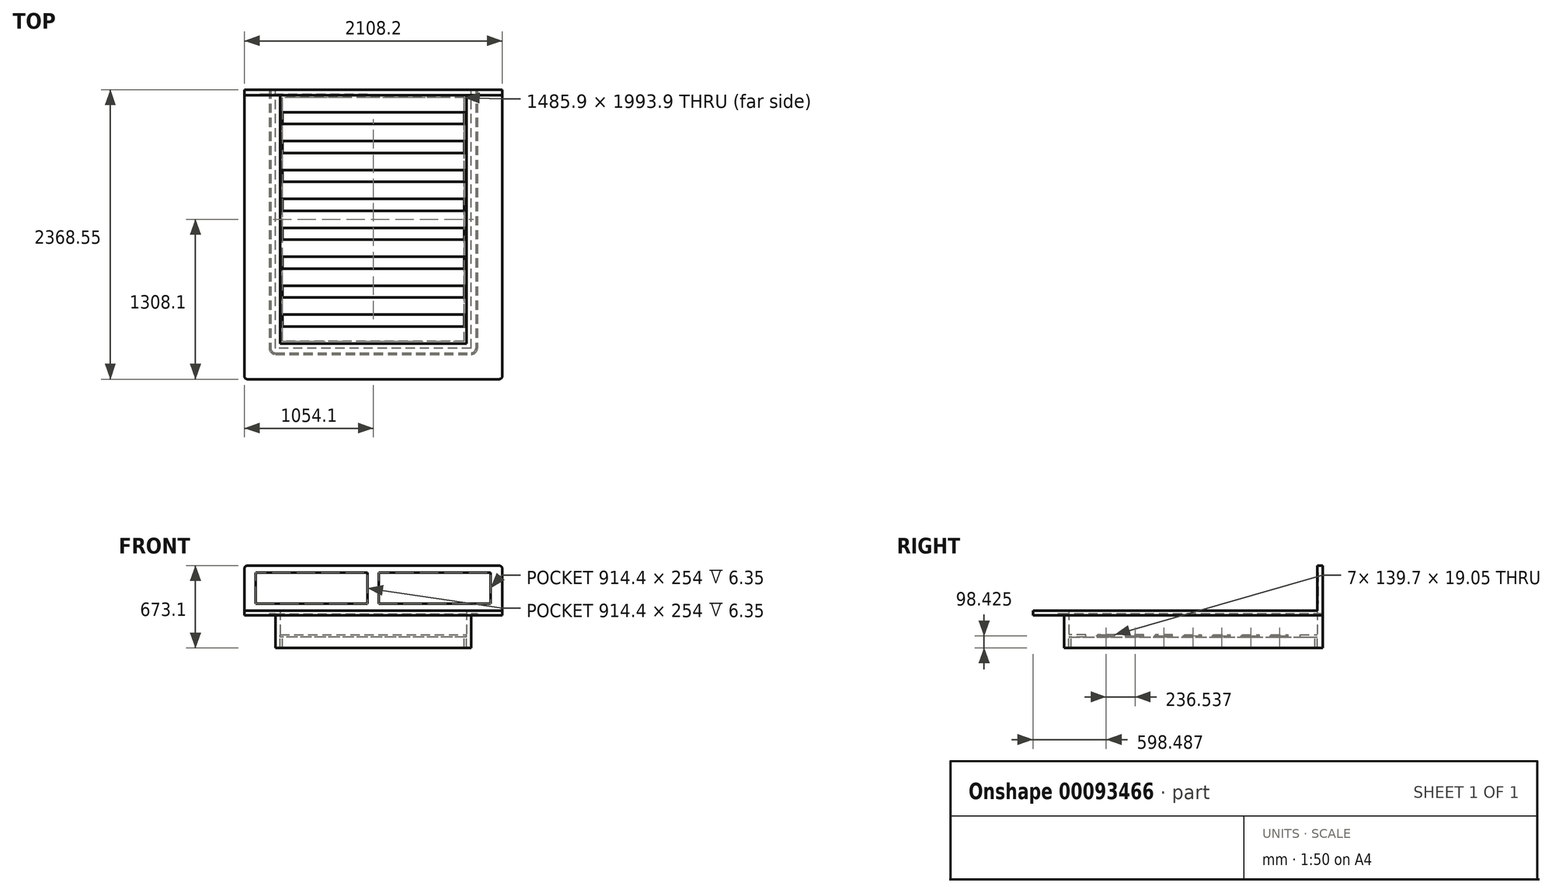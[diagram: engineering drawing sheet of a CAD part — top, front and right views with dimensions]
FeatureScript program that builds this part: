
annotation { "Feature Type Name" : "Feature", "Feature Type Description" : "" }
export const myFeature = defineFeature(function(context is Context, id is Id, definition is map)
    precondition{}
    {
        {
            var Q0;
            Q0=qCreatedBy(makeId("Top.planeOp"),FACE);
            var sketch = newSketch(context, id + "F0", { "sketchPlane" : qUnion([Q0])});
            skLineSegment(sketch, "E0.bottom", {"start": v(762, -1016) * mm, "end": v(-762, -1016) * mm});
            skLineSegment(sketch, "E0.top", {"start": v(762, 1016) * mm, "end": v(-762, 1016) * mm});
            skLineSegment(sketch, "E0.left", {"start": v(762, -1016) * mm, "end": v(762, 1016) * mm});
            skLineSegment(sketch, "E0.right", {"start": v(-762, -1016) * mm, "end": v(-762, 1016) * mm});
            skPoint(sketch, "E0.middle", {"position": v(0, 0) * mm});
            skLineSegment(sketch, "E1.bottom", {"start": v(800.1, -1054.1) * mm, "end": v(-800.1, -1054.1) * mm});
            skLineSegment(sketch, "E1.top", {"start": v(800.1, 1054.1) * mm, "end": v(-800.1, 1054.1) * mm});
            skLineSegment(sketch, "E1.left", {"start": v(800.1, -1054.1) * mm, "end": v(800.1, 1054.1) * mm});
            skLineSegment(sketch, "E1.right", {"start": v(-800.1, -1054.1) * mm, "end": v(-800.1, 1054.1) * mm});
            skSolve(sketch);
        }
        {
            var Q0;
            Q0=makeQuery(id+"F0.imprint","IMPRINT",FACE,{"disambiguationData":[TD([[makeQuery(id+"F0.imprint","IMPRINT",EDGE,{"derivedFrom":sQuery(id+"F0.wireOp",EDGE,"E0.bottom")}),1.0]])]});
            extrude(context, id + "F1", {"entities" : qUnion([Q0]), "depth" : 196.85 * mm, "hasSecondDirection" : true, "secondDirectionOppositeDirection" : true, "secondDirectionDepth" : 107.95 * mm});
        }
        {
            var Q0;
            Q0=qCreatedBy(makeId("Top.planeOp"),FACE);
            var sketch = newSketch(context, id + "F2", { "sketchPlane" : qUnion([Q0])});
            skLineSegment(sketch, "E2.bottom", {"start": v(762, -1016) * mm, "end": v(-762, -1016) * mm});
            skLineSegment(sketch, "E2.top", {"start": v(762, 1016) * mm, "end": v(-762, 1016) * mm});
            skLineSegment(sketch, "E2.left", {"start": v(762, -1016) * mm, "end": v(762, 1016) * mm});
            skLineSegment(sketch, "E2.right", {"start": v(-762, -1016) * mm, "end": v(-762, 1016) * mm});
            skPoint(sketch, "E2.middle", {"position": v(0, 0) * mm});
            skLineSegment(sketch, "E3.bottom", {"start": v(742.95, -996.95) * mm, "end": v(-742.95, -996.95) * mm});
            skLineSegment(sketch, "E3.top", {"start": v(742.95, 996.95) * mm, "end": v(-742.95, 996.95) * mm});
            skLineSegment(sketch, "E3.left", {"start": v(742.95, -996.95) * mm, "end": v(742.95, 996.95) * mm});
            skLineSegment(sketch, "E3.right", {"start": v(-742.95, -996.95) * mm, "end": v(-742.95, 996.95) * mm});
            skPoint(sketch, "E4", {"position": v(-254, 996.95) * mm});
            skPoint(sketch, "E5", {"position": v(254, 996.95) * mm});
            skLineSegment(sketch, "E6", {"start": v(-254, 996.95) * mm, "end": v(-254, -996.95) * mm, "construction": true});
            skLineSegment(sketch, "E7", {"start": v(254, 996.95) * mm, "end": v(254, -996.95) * mm, "construction": true});
            skLineSegment(sketch, "E8.bottom", {"start": v(-244.48, -996.95) * mm, "end": v(-263.53, -996.95) * mm});
            skLineSegment(sketch, "E8.top", {"start": v(-244.48, 996.95) * mm, "end": v(-263.53, 996.95) * mm});
            skLineSegment(sketch, "E8.left", {"start": v(-244.48, -996.95) * mm, "end": v(-244.48, 996.95) * mm});
            skLineSegment(sketch, "E8.right", {"start": v(-263.53, -996.95) * mm, "end": v(-263.53, 996.95) * mm});
            skPoint(sketch, "E8.middle", {"position": v(-254, 0) * mm});
            skLineSegment(sketch, "E9.bottom", {"start": v(263.52, -996.95) * mm, "end": v(244.47, -996.95) * mm});
            skLineSegment(sketch, "E9.top", {"start": v(263.52, 996.95) * mm, "end": v(244.47, 996.95) * mm});
            skLineSegment(sketch, "E9.left", {"start": v(263.52, -996.95) * mm, "end": v(263.52, 996.95) * mm});
            skLineSegment(sketch, "E9.right", {"start": v(244.47, -996.95) * mm, "end": v(244.47, 996.95) * mm});
            skPoint(sketch, "E9.middle", {"position": v(254, 0) * mm});
            skSolve(sketch);
        }
        {
            var Q0;
            Q0=makeQuery(id+"F2.imprint","IMPRINT",FACE,{"disambiguationData":[TD([[makeQuery(id+"F2.imprint","IMPRINT",EDGE,{"derivedFrom":sQuery(id+"F2.wireOp",EDGE,"E2.bottom")}),-1.0]])]});
            var Q1;
            Q1=makeQuery(id+"F2.imprint","IMPRINT",FACE,{"disambiguationData":[TD([[makeQuery(id+"F2.imprint","IMPRINT",EDGE,{"derivedFrom":sQuery(id+"F2.wireOp",EDGE,"E8.bottom")}),-1.0]])]});
            var Q2;
            Q2=makeQuery(id+"F2.imprint","IMPRINT",FACE,{"disambiguationData":[TD([[makeQuery(id+"F2.imprint","IMPRINT",EDGE,{"derivedFrom":sQuery(id+"F2.wireOp",EDGE,"E9.bottom")}),-1.0]])]});
            extrude(context, id + "F3", {"entities" : qUnion([Q0, Q1, Q2]), "oppositeDirection" : true, "depth" : 107.95 * mm});
        }
        {
            var Q0;
            Q0=makeQuery(id+"F3.opExtrude","CAP_FACE",FACE,{"disambiguationData":[OSD([sQuery(id+"F2.wireOp",EDGE,"E2.bottom"),sQuery(id+"F2.wireOp",EDGE,"E2.top"),sQuery(id+"F2.wireOp",EDGE,"E2.left"),sQuery(id+"F2.wireOp",EDGE,"E2.right"),sQuery(id+"F2.wireOp",EDGE,"E3.bottom"),sQuery(id+"F2.wireOp",EDGE,"E3.top"),sQuery(id+"F2.wireOp",EDGE,"E3.left"),sQuery(id+"F2.wireOp",EDGE,"E3.right")])],"isStart":true});
            extrude(context, id + "F4", {"entities" : qUnion([Q0]), "operationType" : NewBodyOperationType.REMOVE, "oppositeDirection" : true, "depth" : 19.05 * mm});
        }
        {
            var Q0;
            Q0=qCreatedBy(makeId("Top.planeOp"),FACE);
            var sketch = newSketch(context, id + "F5", { "sketchPlane" : qUnion([Q0])});
            skLineSegment(sketch, "E10.bottom", {"start": v(-762, 876.3) * mm, "end": v(762, 876.3) * mm});
            skLineSegment(sketch, "E10.top", {"start": v(-762, 1016) * mm, "end": v(762, 1016) * mm});
            skLineSegment(sketch, "E10.left", {"start": v(-762, 876.3) * mm, "end": v(-762, 1016) * mm});
            skLineSegment(sketch, "E10.right", {"start": v(762, 876.3) * mm, "end": v(762, 1016) * mm});
            skPoint(sketch, "E10.middle", {"position": v(0, 946.15) * mm});
            skLineSegment(sketch, "E11.bottom", {"start": v(762, -69.85) * mm, "end": v(-762, -69.85) * mm});
            skLineSegment(sketch, "E11.top", {"start": v(762, 69.85) * mm, "end": v(-762, 69.85) * mm});
            skLineSegment(sketch, "E11.left", {"start": v(762, -69.85) * mm, "end": v(762, 69.85) * mm});
            skLineSegment(sketch, "E11.right", {"start": v(-762, -69.85) * mm, "end": v(-762, 69.85) * mm});
            skPoint(sketch, "E11.middle", {"position": v(0, 0) * mm});
            skLineSegment(sketch, "E12.bottom", {"start": v(762, 403.23) * mm, "end": v(-762, 403.22) * mm});
            skLineSegment(sketch, "E12.top", {"start": v(762, 542.93) * mm, "end": v(-762, 542.92) * mm});
            skLineSegment(sketch, "E12.left", {"start": v(762, 403.23) * mm, "end": v(762, 542.93) * mm});
            skLineSegment(sketch, "E12.right", {"start": v(-762, 403.22) * mm, "end": v(-762, 542.92) * mm});
            skPoint(sketch, "E12.middle", {"position": v(0, 473.08) * mm});
            skLineSegment(sketch, "E13.bottom", {"start": v(762, 639.76) * mm, "end": v(-762, 639.76) * mm});
            skLineSegment(sketch, "E13.top", {"start": v(762, 779.46) * mm, "end": v(-762, 779.46) * mm});
            skLineSegment(sketch, "E13.left", {"start": v(762, 639.76) * mm, "end": v(762, 779.46) * mm});
            skLineSegment(sketch, "E13.right", {"start": v(-762, 639.76) * mm, "end": v(-762, 779.46) * mm});
            skPoint(sketch, "E13.middle", {"position": v(0, 709.61) * mm});
            skLineSegment(sketch, "E14.bottom", {"start": v(762, 166.69) * mm, "end": v(-762, 166.69) * mm});
            skLineSegment(sketch, "E14.top", {"start": v(762, 306.39) * mm, "end": v(-762, 306.39) * mm});
            skLineSegment(sketch, "E14.left", {"start": v(762, 166.69) * mm, "end": v(762, 306.39) * mm});
            skLineSegment(sketch, "E14.right", {"start": v(-762, 166.69) * mm, "end": v(-762, 306.39) * mm});
            skPoint(sketch, "E14.middle", {"position": v(0, 236.54) * mm});
            skLineSegment(sketch, "E15", {"start": v(-925.86, 0) * mm, "end": v(1107.22, 0) * mm, "construction": true});
            skLineSegment(sketch, "E16.MirrorCS", {"start": v(-762, -639.76) * mm, "end": v(-762, -779.46) * mm});
            skLineSegment(sketch, "E17.MirrorCS", {"start": v(762, -639.76) * mm, "end": v(762, -779.46) * mm});
            skLineSegment(sketch, "E18.MirrorCS", {"start": v(762, -779.46) * mm, "end": v(-762, -779.46) * mm});
            skLineSegment(sketch, "E19.MirrorCS", {"start": v(762, -166.69) * mm, "end": v(-762, -166.69) * mm});
            skPoint(sketch, "E20.MirrorP", {"position": v(0, -709.61) * mm});
            skLineSegment(sketch, "E21.MirrorCS", {"start": v(-762, -1016) * mm, "end": v(762, -1016) * mm});
            skLineSegment(sketch, "E22.MirrorCS", {"start": v(762, -166.69) * mm, "end": v(762, -306.39) * mm});
            skLineSegment(sketch, "E23.MirrorCS", {"start": v(-762, -876.3) * mm, "end": v(-762, -1016) * mm});
            skLineSegment(sketch, "E24.MirrorCS", {"start": v(762, -876.3) * mm, "end": v(762, -1016) * mm});
            skLineSegment(sketch, "E25.MirrorCS", {"start": v(-762, -166.69) * mm, "end": v(-762, -306.39) * mm});
            skLineSegment(sketch, "E26.MirrorCS", {"start": v(762, -639.76) * mm, "end": v(-762, -639.76) * mm});
            skPoint(sketch, "E27.MirrorP", {"position": v(0, -946.15) * mm});
            skPoint(sketch, "E28.MirrorP", {"position": v(0, -473.08) * mm});
            skLineSegment(sketch, "E29.MirrorCS", {"start": v(762, -306.39) * mm, "end": v(-762, -306.39) * mm});
            skLineSegment(sketch, "E30.MirrorCS", {"start": v(-762, -403.22) * mm, "end": v(-762, -542.92) * mm});
            skPoint(sketch, "E31.MirrorP", {"position": v(0, -236.54) * mm});
            skLineSegment(sketch, "E32.MirrorCS", {"start": v(762, -403.23) * mm, "end": v(-762, -403.22) * mm});
            skLineSegment(sketch, "E33.MirrorCS", {"start": v(762, -542.93) * mm, "end": v(-762, -542.92) * mm});
            skLineSegment(sketch, "E34.MirrorCS", {"start": v(762, -403.23) * mm, "end": v(762, -542.93) * mm});
            skLineSegment(sketch, "E35.MirrorCS", {"start": v(-762, -876.3) * mm, "end": v(762, -876.3) * mm});
            skSolve(sketch);
        }
        {
            var Q0;
            Q0=makeQuery(id+"F5.imprint","IMPRINT",FACE,{"disambiguationData":[TD([[makeQuery(id+"F5.imprint","IMPRINT",EDGE,{"derivedFrom":sQuery(id+"F5.wireOp",EDGE,"E10.bottom")}),1.0]])]});
            var Q1;
            Q1=makeQuery(id+"F5.imprint","IMPRINT",FACE,{"disambiguationData":[TD([[makeQuery(id+"F5.imprint","IMPRINT",EDGE,{"derivedFrom":sQuery(id+"F5.wireOp",EDGE,"E13.bottom")}),-1.0]])]});
            var Q2;
            Q2=makeQuery(id+"F5.imprint","IMPRINT",FACE,{"disambiguationData":[TD([[makeQuery(id+"F5.imprint","IMPRINT",EDGE,{"derivedFrom":sQuery(id+"F5.wireOp",EDGE,"E12.bottom")}),-1.0]])]});
            var Q3;
            Q3=makeQuery(id+"F5.imprint","IMPRINT",FACE,{"disambiguationData":[TD([[makeQuery(id+"F5.imprint","IMPRINT",EDGE,{"derivedFrom":sQuery(id+"F5.wireOp",EDGE,"E14.bottom")}),-1.0]])]});
            var Q4;
            Q4=makeQuery(id+"F5.imprint","IMPRINT",FACE,{"disambiguationData":[TD([[makeQuery(id+"F5.imprint","IMPRINT",EDGE,{"derivedFrom":sQuery(id+"F5.wireOp",EDGE,"E11.bottom")}),-1.0]])]});
            var Q5;
            Q5=makeQuery(id+"F5.imprint","IMPRINT",FACE,{"disambiguationData":[TD([[makeQuery(id+"F5.imprint","IMPRINT",EDGE,{"derivedFrom":sQuery(id+"F5.wireOp",EDGE,"E19.MirrorCS")}),1.0]])]});
            var Q6;
            Q6=makeQuery(id+"F5.imprint","IMPRINT",FACE,{"disambiguationData":[TD([[makeQuery(id+"F5.imprint","IMPRINT",EDGE,{"derivedFrom":sQuery(id+"F5.wireOp",EDGE,"E30.MirrorCS")}),1.0]])]});
            var Q7;
            Q7=makeQuery(id+"F5.imprint","IMPRINT",FACE,{"disambiguationData":[TD([[makeQuery(id+"F5.imprint","IMPRINT",EDGE,{"derivedFrom":sQuery(id+"F5.wireOp",EDGE,"E16.MirrorCS")}),1.0]])]});
            var Q8;
            Q8=makeQuery(id+"F5.imprint","IMPRINT",FACE,{"disambiguationData":[TD([[makeQuery(id+"F5.imprint","IMPRINT",EDGE,{"derivedFrom":sQuery(id+"F5.wireOp",EDGE,"E21.MirrorCS")}),1.0]])]});
            extrude(context, id + "F6", {"entities" : qUnion([Q0, Q1, Q2, Q3, Q4, Q5, Q6, Q7, Q8]), "oppositeDirection" : true, "depth" : 19.05 * mm});
        }
        {
            var Q0;
            Q0=makeQuery(id+"F1.opExtrude","CAP_FACE",FACE,{"disambiguationData":[OSD([sQuery(id+"F0.wireOp",EDGE,"E0.bottom"),sQuery(id+"F0.wireOp",EDGE,"E0.top"),sQuery(id+"F0.wireOp",EDGE,"E0.left"),sQuery(id+"F0.wireOp",EDGE,"E0.right"),sQuery(id+"F0.wireOp",EDGE,"E1.bottom"),sQuery(id+"F0.wireOp",EDGE,"E1.top"),sQuery(id+"F0.wireOp",EDGE,"E1.left"),sQuery(id+"F0.wireOp",EDGE,"E1.right")])],"isStart":false});
            var sketch = newSketch(context, id + "F7", { "sketchPlane" : qUnion([Q0])});
            skLineSegment(sketch, "E36.bottom", {"start": v(-1054.1, 1054.1) * mm, "end": v(1054.1, 1054.1) * mm});
            skLineSegment(sketch, "E36.top", {"start": v(-1054.1, 1016) * mm, "end": v(1054.1, 1016) * mm});
            skLineSegment(sketch, "E36.left", {"start": v(-1054.1, 1054.1) * mm, "end": v(-1054.1, 1016) * mm});
            skLineSegment(sketch, "E36.right", {"start": v(1054.1, 1054.1) * mm, "end": v(1054.1, 1016) * mm});
            skSolve(sketch);
        }
        {
            var Q0;
            {var subQ3=sQuery(id+"F7.wireOp",EDGE,"E36.right");Q0=makeQuery(id+"F7.imprint","IMPRINT",FACE,{"disambiguationData":[TD([[makeQuery(id+"F7.imprint","IMPRINT",EDGE,{"derivedFrom":subQ3}),-1.0]])]});}
            var Q1;
            {var subQ3=sQuery(id+"F7.wireOp",EDGE,"E36.left");Q1=makeQuery(id+"F7.imprint","IMPRINT",FACE,{"disambiguationData":[TD([[makeQuery(id+"F7.imprint","IMPRINT",EDGE,{"derivedFrom":subQ3}),1.0]])]});}
            var Q2;
            {var subQ2=makeQuery(id+"F1.opExtrude","CAP_EDGE",EDGE,{"disambiguationData":[OSD([sQuery(id+"F0.wireOp",EDGE,"E1.left")])],"isStart":false});var subQ5=makeQuery(id+"F1.opExtrude","CAP_EDGE",EDGE,{"disambiguationData":[OSD([sQuery(id+"F0.wireOp",EDGE,"E1.right")])],"isStart":false});var subQ7=sQuery(id+"F7.wireOp",EDGE,"E36.bottom");var subQ8=makeQuery(id+"F7.imprint","INTERSECT",VERTEX,{"derivedFrom":[subQ2,subQ7]});var subQ9=makeQuery(id+"F7.imprint","INTERSECT",VERTEX,{"derivedFrom":[subQ5,subQ7]});Q2=makeQuery(id+"F7.imprint","IMPRINT",FACE,{"disambiguationData":[TD([[makeQuery(id+"F7.imprint","IMPRINT",EDGE,{"disambiguationData":[TD([[subQ8,-1.0],[subQ9,1.0]])],"derivedFrom":subQ7}),1.0]])]});}
            extrude(context, id + "F8", {"entities" : qUnion([Q0, Q1, Q2]), "operationType" : NewBodyOperationType.ADD, "depth" : 368.3 * mm});
        }
        {
            var Q0;
            Q0=qCreatedBy(makeId("Top.planeOp"),FACE);
            var sketch = newSketch(context, id + "F9", { "sketchPlane" : qUnion([Q0])});
            skLineSegment(sketch, "E37.bottom", {"start": v(762, -1016) * mm, "end": v(-762, -1016) * mm});
            skLineSegment(sketch, "E37.top", {"start": v(762, 1016) * mm, "end": v(-762, 1016) * mm});
            skLineSegment(sketch, "E37.left", {"start": v(762, -1016) * mm, "end": v(762, 1016) * mm});
            skLineSegment(sketch, "E37.right", {"start": v(-762, -1016) * mm, "end": v(-762, 1016) * mm});
            skPoint(sketch, "E37.middle", {"position": v(0, 0) * mm});
            skLineSegment(sketch, "E38.bottom", {"start": v(-1054.1, 1016) * mm, "end": v(1054.1, 1016) * mm});
            skLineSegment(sketch, "E38.top", {"start": v(-1054.1, -1308.1) * mm, "end": v(1054.1, -1308.1) * mm});
            skLineSegment(sketch, "E38.left", {"start": v(-1054.1, 1016) * mm, "end": v(-1054.1, -1308.1) * mm});
            skLineSegment(sketch, "E38.right", {"start": v(1054.1, 1016) * mm, "end": v(1054.1, -1308.1) * mm});
            skSolve(sketch);
        }
        {
            var Q0;
            Q0=makeQuery(id+"F9.imprint","IMPRINT",FACE,{"disambiguationData":[TD([[makeQuery(id+"F9.imprint","IMPRINT",EDGE,{"derivedFrom":sQuery(id+"F9.wireOp",EDGE,"E37.bottom")}),1.0]])]});
            extrude(context, id + "F10", {"entities" : qUnion([Q0]), "operationType" : NewBodyOperationType.ADD, "depth" : 196.93 * mm});
        }
        {
            var Q0;
            Q0=makeQuery(id+"F10.opExtrude","CAP_FACE",FACE,{"disambiguationData":[OSD([sQuery(id+"F9.wireOp",EDGE,"E37.bottom"),sQuery(id+"F9.wireOp",EDGE,"E37.left"),sQuery(id+"F9.wireOp",EDGE,"E37.right"),sQuery(id+"F9.wireOp",EDGE,"E38.bottom"),sQuery(id+"F9.wireOp",EDGE,"E38.top"),sQuery(id+"F9.wireOp",EDGE,"E38.left"),sQuery(id+"F9.wireOp",EDGE,"E38.right")])],"isStart":true});
            extrude(context, id + "F11", {"entities" : qUnion([Q0]), "operationType" : NewBodyOperationType.REMOVE, "oppositeDirection" : true, "depth" : 158.75 * mm});
        }
        {
            var Q0;
            {var subQ0=sQuery(id+"F0.wireOp",EDGE,"E1.right");var subQ2=sQuery(id+"F7.wireOp",EDGE,"E36.top");var subQ4=sQuery(id+"F7.wireOp",EDGE,"E36.bottom");var subQ5=sQuery(id+"F7.wireOp",EDGE,"E36.left");Q0=makeQuery(id+"F8.boolean.opBoolean","SPLIT",FACE,{"disambiguationData":[TD([makeQuery(id+"F1.opExtrude","SWEPT_FACE",FACE,{"disambiguationData":[OSD([subQ0])]})])],"derivedFrom":makeQuery(id+"F8.opExtrude","CAP_FACE",FACE,{"disambiguationData":[OSD([subQ4,subQ2,subQ5,sQuery(id+"F7.wireOp",EDGE,"E36.right")])],"isStart":true})});}
            var Q1;
            {var subQ0=sQuery(id+"F0.wireOp",EDGE,"E1.left");var subQ1=sQuery(id+"F7.wireOp",EDGE,"E36.bottom");var subQ3=sQuery(id+"F7.wireOp",EDGE,"E36.top");var subQ5=sQuery(id+"F7.wireOp",EDGE,"E36.right");Q1=makeQuery(id+"F8.boolean.opBoolean","SPLIT",FACE,{"disambiguationData":[TD([makeQuery(id+"F1.opExtrude","SWEPT_FACE",FACE,{"disambiguationData":[OSD([subQ0])]})])],"derivedFrom":makeQuery(id+"F8.opExtrude","CAP_FACE",FACE,{"disambiguationData":[OSD([subQ1,subQ3,sQuery(id+"F7.wireOp",EDGE,"E36.left"),subQ5])],"isStart":true})});}
            extrude(context, id + "F12", {"entities" : qUnion([Q0, Q1]), "operationType" : NewBodyOperationType.ADD, "depth" : 38.1 * mm});
        }
        {
            var Q0;
            Q0=makeQuery(id+"F10.opExtrude","SWEPT_EDGE",EDGE,{"disambiguationData":[OSD([sQuery(id+"F9.wireOp",EDGE,"E38.top"),sQuery(id+"F9.wireOp",EDGE,"E38.left")])]});
            var Q1;
            Q1=makeQuery(id+"F10.opExtrude","SWEPT_EDGE",EDGE,{"disambiguationData":[OSD([sQuery(id+"F9.wireOp",EDGE,"E38.top"),sQuery(id+"F9.wireOp",EDGE,"E38.right")])]});
            fillet(context, id + "F13", {"entities" : qUnion([Q0, Q1]), "radius" : 25.4 * mm, "tangentPropagation" : true, "allowEdgeOverflow" : false});
        }
        {
            var Q0;
            Q0=makeQuery(id+"F8.opExtrude","CAP_EDGE",EDGE,{"disambiguationData":[OSD([sQuery(id+"F7.wireOp",EDGE,"E36.left")])],"isStart":false});
            var Q1;
            Q1=makeQuery(id+"F8.opExtrude","CAP_EDGE",EDGE,{"disambiguationData":[OSD([sQuery(id+"F7.wireOp",EDGE,"E36.right")])],"isStart":false});
            fillet(context, id + "F14", {"entities" : qUnion([Q0, Q1]), "radius" : 25.4 * mm, "tangentPropagation" : true, "allowEdgeOverflow" : false});
        }
        {
            var Q0;
            {var subQ1=sQuery(id+"F7.wireOp",EDGE,"E36.left");var subQ2=sQuery(id+"F7.wireOp",EDGE,"E36.top");Q0=makeQuery(id+"F10.boolean.opBoolean","SPLIT",FACE,{"disambiguationData":[TD([makeQuery(id+"F8.opExtrude","SWEPT_FACE",FACE,{"disambiguationData":[OSD([subQ1])]})])],"derivedFrom":makeQuery(id+"F8.boolean.opBoolean","MERGE",FACE,{"derivedFrom":[makeQuery(id+"F1.opExtrude","SWEPT_FACE",FACE,{"disambiguationData":[OSD([sQuery(id+"F0.wireOp",EDGE,"E0.top")])]}),makeQuery(id+"F8.opExtrude","SWEPT_FACE",FACE,{"disambiguationData":[OSD([subQ2])]})]})});}
            var sketch = newSketch(context, id + "F15", { "sketchPlane" : qUnion([Q0])});
            skLineSegment(sketch, "E39", {"start": v(0, 565.15) * mm, "end": v(0, 254) * mm, "construction": true});
            skLineSegment(sketch, "E40.bottom", {"start": v(-46.04, 508) * mm, "end": v(-960.44, 508) * mm});
            skLineSegment(sketch, "E40.top", {"start": v(-46.04, 254) * mm, "end": v(-960.44, 254) * mm});
            skLineSegment(sketch, "E40.left", {"start": v(-46.04, 508) * mm, "end": v(-46.04, 254) * mm});
            skLineSegment(sketch, "E40.right", {"start": v(-960.44, 508) * mm, "end": v(-960.44, 254) * mm});
            skLineSegment(sketch, "E41.MirrorCS", {"start": v(46.04, 508) * mm, "end": v(960.44, 508) * mm});
            skLineSegment(sketch, "E42.MirrorCS", {"start": v(46.04, 254) * mm, "end": v(960.44, 254) * mm});
            skLineSegment(sketch, "E43.MirrorCS", {"start": v(46.04, 508) * mm, "end": v(46.04, 254) * mm});
            skLineSegment(sketch, "E44.MirrorCS", {"start": v(960.44, 508) * mm, "end": v(960.44, 254) * mm});
            skSolve(sketch);
        }
        {
            var Q0;
            Q0=makeQuery(id+"F15.imprint","IMPRINT",FACE,{"disambiguationData":[TD([[makeQuery(id+"F15.imprint","IMPRINT",EDGE,{"derivedFrom":sQuery(id+"F15.wireOp",EDGE,"E40.bottom")}),-1.0]])]});
            var Q1;
            Q1=makeQuery(id+"F15.imprint","IMPRINT",FACE,{"disambiguationData":[TD([[makeQuery(id+"F15.imprint","IMPRINT",EDGE,{"derivedFrom":sQuery(id+"F15.wireOp",EDGE,"E41.MirrorCS")}),-1.0]])]});
            var Q2;
            Q2=makeQuery(id+"F15.imprint","IMPRINT",FACE,{"disambiguationData":[TD([[makeQuery(id+"F15.imprint","IMPRINT",EDGE,{"derivedFrom":sQuery(id+"F15.wireOp",EDGE,"E40.bottom")}),1.0]])]});
            extrude(context, id + "F16", {"entities" : qUnion([Q0, Q1, Q2]), "operationType" : NewBodyOperationType.ADD, "oppositeDirection" : true, "depth" : 44.45 * mm});
        }
        {
            var Q0;
            Q0=makeQuery(id+"F15.imprint","IMPRINT",FACE,{"disambiguationData":[TD([[makeQuery(id+"F15.imprint","IMPRINT",EDGE,{"derivedFrom":sQuery(id+"F15.wireOp",EDGE,"E40.bottom")}),1.0]])]});
            var Q1;
            Q1=makeQuery(id+"F15.imprint","IMPRINT",FACE,{"disambiguationData":[TD([[makeQuery(id+"F15.imprint","IMPRINT",EDGE,{"derivedFrom":sQuery(id+"F15.wireOp",EDGE,"E41.MirrorCS")}),-1.0]])]});
            extrude(context, id + "F17", {"entities" : qUnion([Q0, Q1]), "operationType" : NewBodyOperationType.REMOVE, "oppositeDirection" : true, "depth" : 6.35 * mm});
        }
        {
            var Q0;
            {var subQ0=sQuery(id+"F7.wireOp",EDGE,"E36.bottom");var subQ1=makeQuery(id+"F8.opExtrude","SWEPT_FACE",FACE,{"disambiguationData":[OSD([subQ0])]});var subQ2=makeQuery(id+"F1.opExtrude","SWEPT_FACE",FACE,{"disambiguationData":[OSD([sQuery(id+"F0.wireOp",EDGE,"E1.top")])]});var subQ6=makeQuery(id+"F8.opExtrude","CAP_EDGE",EDGE,{"disambiguationData":[OSD([subQ0])],"isStart":true});Q0=makeQuery(id+"F12.boolean.opBoolean","MERGE",FACE,{"derivedFrom":[makeQuery(id+"F8.boolean.opBoolean","MERGE",FACE,{"derivedFrom":[subQ2,subQ1]}),makeQuery(id+"F12.opExtrude","SWEPT_FACE",FACE,{"disambiguationData":[OSD([subQ0]),TDD([makeQuery(id+"F8.boolean.opBoolean","SPLIT",EDGE,{"disambiguationData":[TD([makeQuery(id+"F1.opExtrude","SWEPT_FACE",FACE,{"disambiguationData":[OSD([sQuery(id+"F0.wireOp",EDGE,"E1.right")])]})])],"derivedFrom":subQ6})])]}),makeQuery(id+"F12.opExtrude","SWEPT_FACE",FACE,{"disambiguationData":[OSD([subQ0]),TDD([makeQuery(id+"F8.boolean.opBoolean","SPLIT",EDGE,{"disambiguationData":[TD([makeQuery(id+"F1.opExtrude","SWEPT_FACE",FACE,{"disambiguationData":[OSD([sQuery(id+"F0.wireOp",EDGE,"E1.left")])]})])],"derivedFrom":subQ6})])]})]});}
            extrude(context, id + "F18", {"entities" : qUnion([Q0]), "operationType" : NewBodyOperationType.ADD, "depth" : 6.35 * mm});
        }
        {
            var Q0;
            {var subQ0=sQuery(id+"F7.wireOp",EDGE,"E36.bottom");var subQ4=sQuery(id+"F0.wireOp",EDGE,"E1.left");var subQ5=makeQuery(id+"F1.opExtrude","SWEPT_FACE",FACE,{"disambiguationData":[OSD([subQ4])]});var subQ6=sQuery(id+"F7.wireOp",EDGE,"E36.right");var subQ7=sQuery(id+"F7.wireOp",EDGE,"E36.left");var subQ8=sQuery(id+"F7.wireOp",EDGE,"E36.top");var subQ9=makeQuery(id+"F8.opExtrude","CAP_FACE",FACE,{"disambiguationData":[OSD([subQ0,subQ8,subQ7,subQ6])],"isStart":true});var subQ11=makeQuery(id+"F8.opExtrude","CAP_EDGE",EDGE,{"disambiguationData":[OSD([subQ0])],"isStart":true});var subQ12=sQuery(id+"F0.wireOp",EDGE,"E1.right");var subQ13=makeQuery(id+"F1.opExtrude","SWEPT_FACE",FACE,{"disambiguationData":[OSD([subQ12])]});Q0=makeQuery(id+"F18.boolean.opBoolean","MERGE",FACE,{"derivedFrom":[makeQuery(id+"F12.boolean.opBoolean","MERGE",FACE,{"derivedFrom":[makeQuery(id+"F11.boolean.opBoolean","COPY",FACE,{"derivedFrom":makeQuery(id+"F11.opExtrude","CAP_FACE",FACE,{"disambiguationData":[OSD([sQuery(id+"F9.wireOp",EDGE,"E37.bottom"),sQuery(id+"F9.wireOp",EDGE,"E37.left"),sQuery(id+"F9.wireOp",EDGE,"E37.right"),sQuery(id+"F9.wireOp",EDGE,"E38.bottom"),sQuery(id+"F9.wireOp",EDGE,"E38.top"),sQuery(id+"F9.wireOp",EDGE,"E38.left"),sQuery(id+"F9.wireOp",EDGE,"E38.right")])],"isStart":false})}),makeQuery(id+"F12.opExtrude","CAP_FACE",FACE,{"disambiguationData":[OSD([subQ0,subQ8,subQ7,subQ6]),TDD([makeQuery(id+"F8.boolean.opBoolean","SPLIT",FACE,{"disambiguationData":[TD([subQ13])],"derivedFrom":subQ9})])],"isStart":false}),makeQuery(id+"F12.opExtrude","CAP_FACE",FACE,{"disambiguationData":[OSD([subQ0,subQ8,subQ7,subQ6]),TDD([makeQuery(id+"F8.boolean.opBoolean","SPLIT",FACE,{"disambiguationData":[TD([subQ5])],"derivedFrom":subQ9})])],"isStart":false})]}),makeQuery(id+"F18.opExtrude","SWEPT_FACE",FACE,{"disambiguationData":[OSD([subQ0]),TDD([makeQuery(id+"F12.opExtrude","CAP_EDGE",EDGE,{"disambiguationData":[OSD([subQ0]),TDD([makeQuery(id+"F8.boolean.opBoolean","SPLIT",EDGE,{"disambiguationData":[TD([subQ13])],"derivedFrom":subQ11})])],"isStart":false})])]}),makeQuery(id+"F18.opExtrude","SWEPT_FACE",FACE,{"disambiguationData":[OSD([subQ0]),TDD([makeQuery(id+"F12.opExtrude","CAP_EDGE",EDGE,{"disambiguationData":[OSD([subQ0]),TDD([makeQuery(id+"F8.boolean.opBoolean","SPLIT",EDGE,{"disambiguationData":[TD([subQ5])],"derivedFrom":subQ11})])],"isStart":false})])]})]});}
            var sketch = newSketch(context, id + "F19", { "sketchPlane" : qUnion([Q0])});
            skLineSegment(sketch, "E45.bottom", {"start": v(-838.2, -1060.45) * mm, "end": v(838.2, -1060.45) * mm});
            skLineSegment(sketch, "E45.top", {"start": v(-800.1, 1092.2) * mm, "end": v(800.1, 1092.2) * mm});
            skLineSegment(sketch, "E45.left", {"start": v(-838.2, -1060.45) * mm, "end": v(-838.2, 1054.1) * mm});
            skLineSegment(sketch, "E45.right", {"start": v(838.2, -1060.45) * mm, "end": v(838.2, 1054.1) * mm});
            skLineSegment(sketch, "E46.bottom", {"start": v(-850.9, -1060.45) * mm, "end": v(850.9, -1060.45) * mm});
            skLineSegment(sketch, "E46.top", {"start": v(-800.1, 1104.9) * mm, "end": v(800.1, 1104.9) * mm});
            skLineSegment(sketch, "E46.left", {"start": v(-850.9, -1060.45) * mm, "end": v(-850.9, 1054.1) * mm});
            skLineSegment(sketch, "E46.right", {"start": v(850.9, -1060.45) * mm, "end": v(850.9, 1054.1) * mm});
            skPoint(sketch, "E47.visualSharp", {"position": v(-838.2, 1092.2) * mm});
            skArc(sketch, "E47.filletArc", {"start": v(-800.1, 1092.2) * mm, "mid": v(-827.04, 1081.04) * mm, "end": v(-838.2, 1054.1) * mm});
            skPoint(sketch, "E48.visualSharp", {"position": v(838.2, 1092.2) * mm});
            skArc(sketch, "E48.filletArc", {"start": v(838.2, 1054.1) * mm, "mid": v(827.04, 1081.04) * mm, "end": v(800.1, 1092.2) * mm});
            skPoint(sketch, "E49.visualSharp", {"position": v(-850.9, 1104.9) * mm});
            skArc(sketch, "E49.filletArc", {"start": v(-800.1, 1104.9) * mm, "mid": v(-836.02, 1090.02) * mm, "end": v(-850.9, 1054.1) * mm});
            skPoint(sketch, "E50.visualSharp", {"position": v(850.9, 1104.9) * mm});
            skArc(sketch, "E50.filletArc", {"start": v(850.9, 1054.1) * mm, "mid": v(836.02, 1090.02) * mm, "end": v(800.1, 1104.9) * mm});
            skSolve(sketch);
        }
        {
            var Q0;
            Q0=makeQuery(id+"F19.imprint","IMPRINT",FACE,{"disambiguationData":[TD([[makeQuery(id+"F19.imprint","IMPRINT",EDGE,{"derivedFrom":sQuery(id+"F19.wireOp",EDGE,"E45.top")}),1.0]])]});
            extrude(context, id + "F20", {"entities" : qUnion([Q0]), "operationType" : NewBodyOperationType.REMOVE, "oppositeDirection" : true, "depth" : 12.7 * mm});
        }
    });
